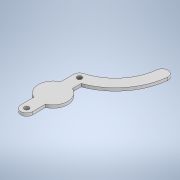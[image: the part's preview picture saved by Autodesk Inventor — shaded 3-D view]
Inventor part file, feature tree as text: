
AUTODESK INVENTOR PART (.ipt)
format: ipt  version: 2021 (Build 250183000, 183)  size: 133,120 bytes
history: native  units: mm
features: other x1, extrude x1, sketch x1
ambient origin geometry x8: Origin, YZ Plane, XZ Plane, XY Plane, X Axis, Y Axis, Z Axis, Center Point
bodies: Solid1 (feature_tree)
feature tree (3):
  other  "<userpath>\Documents\Semestre8\Robótica\Proyecto-Rob\Piezas\ParámetrosGripper.xlsx"
  extrude  "Extrusion1"  Depth=5.0mm
  sketch  "Sketch1"  dims[d0=20.0mm d2=90.0mm d3=8.0mm d4=8.0mm d5=20.0mm d7=100.0mm d8=24.43461mm d9=100.0mm d10=50.0mm d11=5.0mm d12=0.0mm]
